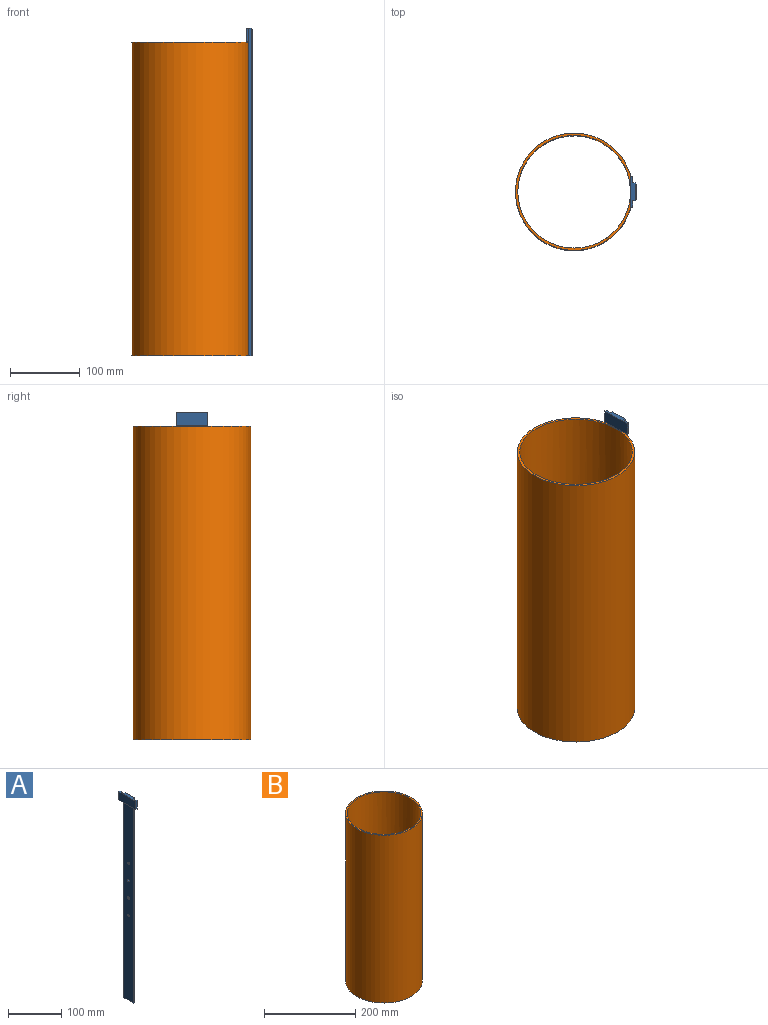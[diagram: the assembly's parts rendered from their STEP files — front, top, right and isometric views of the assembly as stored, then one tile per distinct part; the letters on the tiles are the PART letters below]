
ASSEMBLY  parts=2 mates=1
PART A: 19 faces, bbox 8.2x45x470 mm
  f0: plane 451x25mm, normal (-1,0,0), area 11196.5mm2, adj f1,f2,f3,f6,f7,f8,f9,f15
  f1: plane 470x3mm, normal (0,-1,0), area 1410mm2, adj f0,f2,f4,f10,f18
  f2: plane 25x5mm, normal (0,0,-1), area 121mm2, adj f0,f1,f3,f5,f10,f11
  f3: plane 470x3mm, normal (0,1,0), area 1410mm2, adj f0,f2,f4,f11,f13
  f4: plane 45x6.18mm, normal (0,0,1), area 217.9mm2, adj f1,f3,f12,f13,f14,f16,f17,f18
  f5: plane 468x21mm, normal (1,0,0), area 9749.5mm2, adj f2,f6,f7,f8,f9,f10,f11,f12
  f6: cylinder r=2.5mm len=5mm, axis (-1,0,0), area 78.5mm2, adj f0,f5
  f7: cylinder r=2.5mm len=5mm, axis (-1,0,0), area 78.5mm2, adj f0,f5
  f8: cylinder r=2.5mm len=5mm, axis (-1,0,0), area 78.5mm2, adj f0,f5
  f9: cylinder r=2.5mm len=5mm, axis (-1,0,0), area 78.5mm2, adj f0,f5
  f10: plane 470x2mm, normal (0.71,-0.71,0), area 1326.5mm2, adj f1,f2,f5,f12
  f11: plane 470x2mm, normal (0.71,0.71,0), area 1326.5mm2, adj f2,f3,f5,f12
  f12: plane 25x2mm, normal (0.71,0,0.71), area 65.1mm2, adj f4,f5,f10,f11
  f13: plane 19x10mm, normal (1,0,0), area 190mm2, adj f3,f4,f14,f15
  f14: plane 19x3.18mm, normal (0,1,0), area 60.3mm2, adj f4,f13,f15,f17
  f15: plane 45x3.18mm, normal (0,0,-1), area 142.9mm2, adj f0,f13,f14,f16,f17,f18
  f16: plane 19x3.18mm, normal (0,-1,0), area 60.3mm2, adj f4,f15,f17,f18
  f17: plane 45x19mm, normal (-1,0,0), area 855mm2, adj f4,f14,f15,f16
  f18: plane 19x10mm, normal (1,0,0), area 190mm2, adj f1,f4,f15,f16
PART B: 8 faces, bbox 168.3x168.3x450 mm
  f0: cylinder r=84.14mm len=450mm, axis (0,0,-1), area 237814.4mm2, adj f2,f3,f4,f5,f6,f7
  f1: cylinder r=80.75mm len=450mm, axis (0,0,-1), area 228236.7mm2, adj f2,f3,f4,f5,f6,f7
  f2: plane 168.28x168.28mm, normal (0,0,1), area 1754.8mm2, adj f0,f1
  f3: plane 168.28x168.28mm, normal (0,0,-1), area 1754.8mm2, adj f0,f1
  f4: cylinder r=2.5mm len=5mm, axis (1,0,0), area 53.2mm2, adj f0,f1
  f5: cylinder r=2.5mm len=5mm, axis (1,0,0), area 53.2mm2, adj f0,f1
  f6: cylinder r=2.5mm len=5mm, axis (1,0,0), area 53.2mm2, adj f0,f1
  f7: cylinder r=2.5mm len=5mm, axis (1,0,0), area 53.2mm2, adj f0,f1
PLACE A t=(-588.67,1.76,-244.03)mm
PLACE B t=(-573.04,-10.21,-84.45)mm
MATE fastened A.f9 <-> B.f4  axis (-1,0,0) through (-136.47,-10.21,110.55)mm
